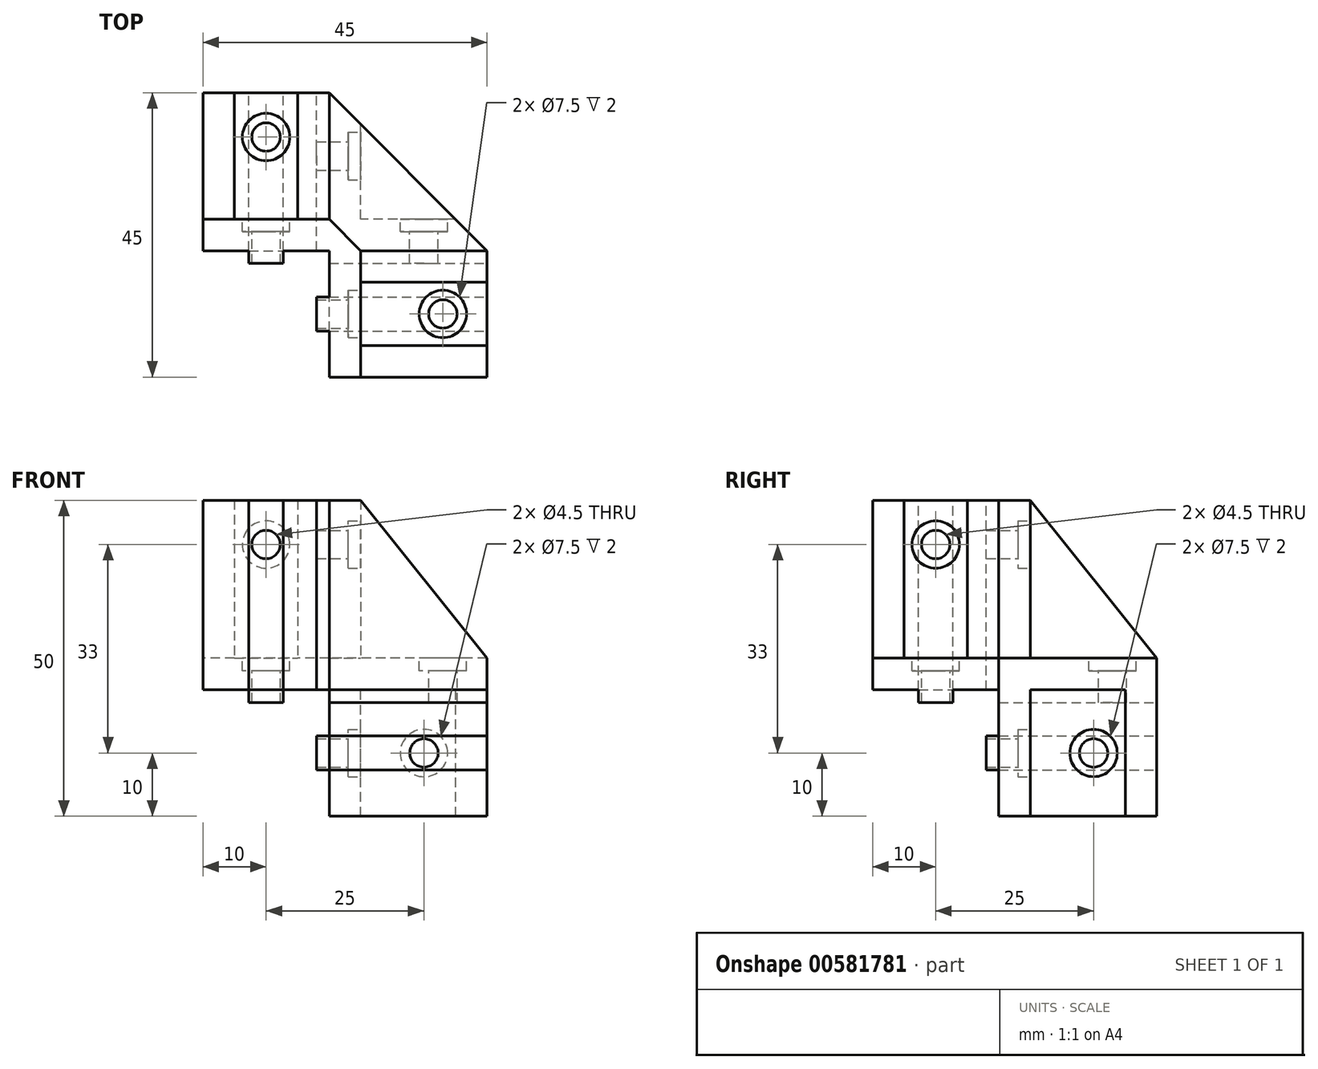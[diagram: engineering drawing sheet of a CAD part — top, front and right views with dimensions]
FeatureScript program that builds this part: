
annotation { "Feature Type Name" : "Feature", "Feature Type Description" : "" }
export const myFeature = defineFeature(function(context is Context, id is Id, definition is map)
    precondition{}
    {
        {
            var Q0;
            Q0=qCreatedBy(makeId("Top.planeOp"),FACE);
            var sketch = newSketch(context, id + "F0", { "sketchPlane" : qUnion([Q0])});
            skLineSegment(sketch, "E0", {"start": v(0, 0) * mm, "end": v(0, 60) * mm, "construction": true});
            skLineSegment(sketch, "E1", {"start": v(0, 60) * mm, "end": v(20, 60) * mm, "construction": true});
            skLineSegment(sketch, "E2", {"start": v(20, 60) * mm, "end": v(20, 20) * mm, "construction": true});
            skLineSegment(sketch, "E3", {"start": v(20, 20) * mm, "end": v(60, 20) * mm, "construction": true});
            skLineSegment(sketch, "E4", {"start": v(60, 20) * mm, "end": v(60, 0) * mm, "construction": true});
            skLineSegment(sketch, "E5", {"start": v(60, 0) * mm, "end": v(0, 0) * mm, "construction": true});
            skLineSegment(sketch, "E6", {"start": v(20, 20) * mm, "end": v(0, 20) * mm});
            skLineSegment(sketch, "E7", {"start": v(0, 20) * mm, "end": v(0, 45) * mm});
            skLineSegment(sketch, "E8", {"start": v(0, 45) * mm, "end": v(20, 45) * mm});
            skLineSegment(sketch, "E9", {"start": v(20, 20) * mm, "end": v(20, 0) * mm});
            skLineSegment(sketch, "E10", {"start": v(20, 0) * mm, "end": v(45, 0) * mm});
            skLineSegment(sketch, "E11", {"start": v(45, 0) * mm, "end": v(45, 20) * mm});
            skPoint(sketch, "E11.endSnap0", {"position": v(40, 20) * mm});
            skLineSegment(sketch, "E12", {"start": v(45, 20) * mm, "end": v(20, 45) * mm});
            skSolve(sketch);
        }
        {
            var Q0;
            Q0=makeQuery(id+"F0.imprint","IMPRINT",FACE,{"disambiguationData":[TD([[makeQuery(id+"F0.imprint","IMPRINT",EDGE,{"derivedFrom":sQuery(id+"F0.wireOp",EDGE,"E6")}),-1.0]])]});
            extrude(context, id + "F1", {"entities" : qUnion([Q0]), "depth" : 5 * mm});
        }
        {
            var Q0;
            Q0=makeQuery(id+"F1.opExtrude","CAP_FACE",FACE,{"disambiguationData":[OSD([sQuery(id+"F0.wireOp",EDGE,"E6"),sQuery(id+"F0.wireOp",EDGE,"E7"),sQuery(id+"F0.wireOp",EDGE,"E8"),sQuery(id+"F0.wireOp",EDGE,"E9"),sQuery(id+"F0.wireOp",EDGE,"E10"),sQuery(id+"F0.wireOp",EDGE,"E11"),sQuery(id+"F0.wireOp",EDGE,"E12")])],"isStart":false});
            var sketch = newSketch(context, id + "F2", { "sketchPlane" : qUnion([Q0])});
            skLineSegment(sketch, "E13", {"start": v(0, 20) * mm, "end": v(0, 25) * mm});
            skLineSegment(sketch, "E14", {"start": v(5, 25) * mm, "end": v(15, 25) * mm});
            skLineSegment(sketch, "E15", {"start": v(25, 15) * mm, "end": v(25, 5) * mm});
            skLineSegment(sketch, "E16", {"start": v(25, 0) * mm, "end": v(20, 0) * mm});
            skLineSegment(sketch, "E17", {"start": v(20, 0) * mm, "end": v(20, 20) * mm});
            skLineSegment(sketch, "E18", {"start": v(20, 20) * mm, "end": v(0, 20) * mm});
            skLineSegment(sketch, "E19", {"start": v(20, 45) * mm, "end": v(20, 25) * mm});
            skLineSegment(sketch, "E20", {"start": v(20, 45) * mm, "end": v(15, 45) * mm});
            skLineSegment(sketch, "E21", {"start": v(15, 45) * mm, "end": v(15, 25) * mm});
            skLineSegment(sketch, "E22", {"start": v(0, 25) * mm, "end": v(0, 45) * mm});
            skLineSegment(sketch, "E23", {"start": v(0, 45) * mm, "end": v(5, 45) * mm});
            skLineSegment(sketch, "E24", {"start": v(5, 45) * mm, "end": v(5, 25) * mm});
            skLineSegment(sketch, "E25", {"start": v(45, 20) * mm, "end": v(25, 20) * mm});
            skLineSegment(sketch, "E26", {"start": v(45, 20) * mm, "end": v(45, 15) * mm});
            skLineSegment(sketch, "E27", {"start": v(45, 15) * mm, "end": v(25, 15) * mm});
            skLineSegment(sketch, "E28", {"start": v(45, 0) * mm, "end": v(45, 5) * mm});
            skLineSegment(sketch, "E29", {"start": v(45, 5) * mm, "end": v(25, 5) * mm});
            skLineSegment(sketch, "E30", {"start": v(45, 0) * mm, "end": v(25, 0) * mm});
            skLineSegment(sketch, "E31", {"start": v(20, 25) * mm, "end": v(25, 20) * mm});
            skSolve(sketch);
        }
        {
            var Q0;
            Q0=qSketchRegion(id+"F2",true);
            extrude(context, id + "F3", {"entities" : qUnion([Q0]), "operationType" : NewBodyOperationType.ADD, "depth" : 25 * mm});
        }
        {
            var Q0;
            Q0=qSketchRegion(id+"F2",true);
            extrude(context, id + "F4", {"entities" : qUnion([Q0]), "operationType" : NewBodyOperationType.ADD, "depth" : 25 * mm});
        }
        {
            var Q0;
            Q0=makeQuery(id+"F3.boolean.opBoolean","MERGE",FACE,{"derivedFrom":[makeQuery(id+"F1.opExtrude","SWEPT_FACE",FACE,{"disambiguationData":[OSD([sQuery(id+"F0.wireOp",EDGE,"E7")])]}),makeQuery(id+"F3.opExtrude","SWEPT_FACE",FACE,{"disambiguationData":[OSD([sQuery(id+"F2.wireOp",EDGE,"E13"),sQuery(id+"F2.wireOp",EDGE,"E22")])]})]});
            var sketch = newSketch(context, id + "F5", { "sketchPlane" : qUnion([Q0])});
            skLineSegment(sketch, "E32", {"start": v(-20, 30) * mm, "end": v(-25, 30) * mm, "construction": true});
            skLineSegment(sketch, "E33", {"start": v(-45, 0) * mm, "end": v(-45, 5) * mm, "construction": true});
            skLineSegment(sketch, "E34", {"start": v(-45, 5) * mm, "end": v(-25, 30) * mm});
            skLineSegment(sketch, "E35", {"start": v(-25, 30) * mm, "end": v(-45, 30) * mm});
            skLineSegment(sketch, "E36", {"start": v(-45, 30) * mm, "end": v(-45, 5) * mm});
            skSolve(sketch);
        }
        {
            var Q0;
            Q0=qSketchRegion(id+"F5",true);
            extrude(context, id + "F6", {"entities" : qUnion([Q0]), "operationType" : NewBodyOperationType.REMOVE, "endBound" : BoundingType.THROUGH_ALL, "oppositeDirection" : true, "depth" : 25 * mm});
        }
        {
            var Q0;
            {var subQ0=sQuery(id+"F0.wireOp",EDGE,"E6");var subQ1=sQuery(id+"F11.wireOp",EDGE,"E47");var subQ2=sQuery(id+"F11.wireOp",EDGE,"E46");var subQ3=sQuery(id+"F11.wireOp",EDGE,"E45");var subQ4=makeQuery(id+"F12.opExtrude","CAP_FACE",FACE,{"disambiguationData":[OSD([sQuery(id+"F11.wireOp",EDGE,"E44"),subQ3,subQ2,subQ1,sQuery(id+"F11.wireOp",EDGE,"E48")])],"isStart":false});var subQ5=sQuery(id+"F0.wireOp",EDGE,"E9");var subQ6=sQuery(id+"F0.wireOp",EDGE,"E12");var subQ7=sQuery(id+"F0.wireOp",EDGE,"E8");var subQ8=sQuery(id+"F0.wireOp",EDGE,"E7");var subQ9=makeQuery(id+"F1.opExtrude","CAP_FACE",FACE,{"disambiguationData":[OSD([subQ0,subQ8,subQ7,subQ5,sQuery(id+"F0.wireOp",EDGE,"E10"),sQuery(id+"F0.wireOp",EDGE,"E11"),subQ6])],"isStart":true});var subQ10=makeQuery(id+"F12.opExtrude","CAP_FACE",FACE,{"disambiguationData":[OSD([sQuery(id+"F11.wireOp",EDGE,"E49"),sQuery(id+"F11.wireOp",EDGE,"E50"),sQuery(id+"F11.wireOp",EDGE,"E51"),sQuery(id+"F11.wireOp",EDGE,"E52"),sQuery(id+"F11.wireOp",EDGE,"E53")])],"isStart":false});Q0=makeQuery(id+"F20.boolean.opBoolean","SPLIT",FACE,{"disambiguationData":[TD([makeQuery(id+"F1.opExtrude","SWEPT_FACE",FACE,{"disambiguationData":[OSD([subQ8])]})])],"derivedFrom":makeQuery(id+"F12.boolean.opBoolean","MERGE",FACE,{"derivedFrom":[subQ9,subQ4,subQ10]})});}
            var sketch = newSketch(context, id + "F7", { "sketchPlane" : qUnion([Q0])});
            skLineSegment(sketch, "E37.bottom", {"start": v(18, -7.29) * mm, "end": v(45, -7.29) * mm});
            skLineSegment(sketch, "E37.top", {"start": v(18, -12.7) * mm, "end": v(45, -12.7) * mm});
            skLineSegment(sketch, "E37.left", {"start": v(18, -7.29) * mm, "end": v(18, -12.7) * mm});
            skLineSegment(sketch, "E37.right", {"start": v(45, -7.29) * mm, "end": v(45, -12.7) * mm});
            skPoint(sketch, "E38.oppositeSnap0", {"position": v(12.71, -19) * mm});
            skLineSegment(sketch, "E38.bottom", {"start": v(7.3, -18) * mm, "end": v(12.71, -18) * mm});
            skLineSegment(sketch, "E38.top", {"start": v(7.3, -45) * mm, "end": v(12.71, -45) * mm});
            skLineSegment(sketch, "E38.left", {"start": v(7.3, -18) * mm, "end": v(7.3, -45) * mm});
            skLineSegment(sketch, "E38.right", {"start": v(12.71, -18) * mm, "end": v(12.71, -45) * mm});
            skSolve(sketch);
        }
        {
            var Q0;
            Q0=qSketchRegion(id+"F7",true);
            extrude(context, id + "F8", {"entities" : qUnion([Q0]), "operationType" : NewBodyOperationType.ADD, "depth" : 2 * mm});
        }
        {
            var Q0;
            Q0=makeQuery(id+"F3.boolean.opBoolean","MERGE",FACE,{"derivedFrom":[makeQuery(id+"F1.opExtrude","SWEPT_FACE",FACE,{"disambiguationData":[OSD([sQuery(id+"F0.wireOp",EDGE,"E10")])]}),makeQuery(id+"F3.opExtrude","SWEPT_FACE",FACE,{"disambiguationData":[OSD([sQuery(id+"F2.wireOp",EDGE,"E16"),sQuery(id+"F2.wireOp",EDGE,"E30")])]})]});
            var sketch = newSketch(context, id + "F9", { "sketchPlane" : qUnion([Q0])});
            skLineSegment(sketch, "E39", {"start": v(20, 30) * mm, "end": v(25, 30) * mm, "construction": true});
            skLineSegment(sketch, "E40", {"start": v(25, 30) * mm, "end": v(45, 5) * mm});
            skLineSegment(sketch, "E41", {"start": v(45, 5) * mm, "end": v(45, 0) * mm, "construction": true});
            skLineSegment(sketch, "E42", {"start": v(25, 30) * mm, "end": v(45, 30) * mm});
            skLineSegment(sketch, "E43", {"start": v(45, 30) * mm, "end": v(45, 5) * mm});
            skSolve(sketch);
        }
        {
            var Q0;
            Q0=qSketchRegion(id+"F9",true);
            extrude(context, id + "F10", {"entities" : qUnion([Q0]), "operationType" : NewBodyOperationType.REMOVE, "endBound" : BoundingType.THROUGH_ALL, "oppositeDirection" : true, "depth" : 25 * mm});
        }
        {
            var Q0;
            Q0=makeQuery(id+"F3.opExtrude","CAP_FACE",FACE,{"disambiguationData":[OSD([sQuery(id+"F2.wireOp",EDGE,"E13"),sQuery(id+"F2.wireOp",EDGE,"E14"),sQuery(id+"F2.wireOp",EDGE,"E15"),sQuery(id+"F2.wireOp",EDGE,"E16"),sQuery(id+"F2.wireOp",EDGE,"E17"),sQuery(id+"F2.wireOp",EDGE,"E18"),sQuery(id+"F2.wireOp",EDGE,"E19"),sQuery(id+"F2.wireOp",EDGE,"E20"),sQuery(id+"F2.wireOp",EDGE,"E21"),sQuery(id+"F2.wireOp",EDGE,"E22"),sQuery(id+"F2.wireOp",EDGE,"E23"),sQuery(id+"F2.wireOp",EDGE,"E24"),sQuery(id+"F2.wireOp",EDGE,"E25"),sQuery(id+"F2.wireOp",EDGE,"E26"),sQuery(id+"F2.wireOp",EDGE,"E27"),sQuery(id+"F2.wireOp",EDGE,"E28"),sQuery(id+"F2.wireOp",EDGE,"E29"),sQuery(id+"F2.wireOp",EDGE,"E30"),sQuery(id+"F2.wireOp",EDGE,"E31")])],"isStart":false});
            var sketch = newSketch(context, id + "F11", { "sketchPlane" : qUnion([Q0])});
            skLineSegment(sketch, "E44", {"start": v(10, 20) * mm, "end": v(12.71, 20) * mm});
            skLineSegment(sketch, "E45", {"start": v(12.71, 20) * mm, "end": v(12.71, 18) * mm});
            skLineSegment(sketch, "E46", {"start": v(12.71, 18) * mm, "end": v(7.3, 18) * mm});
            skLineSegment(sketch, "E47", {"start": v(7.3, 18) * mm, "end": v(7.3, 20) * mm});
            skLineSegment(sketch, "E48", {"start": v(7.3, 20) * mm, "end": v(10, 20) * mm});
            skLineSegment(sketch, "E49", {"start": v(20, 10) * mm, "end": v(20, 12.7) * mm});
            skLineSegment(sketch, "E50", {"start": v(20, 12.7) * mm, "end": v(18, 12.7) * mm});
            skLineSegment(sketch, "E51", {"start": v(18, 12.7) * mm, "end": v(18, 7.29) * mm});
            skLineSegment(sketch, "E52", {"start": v(18, 7.29) * mm, "end": v(20, 7.29) * mm});
            skLineSegment(sketch, "E53", {"start": v(20, 7.29) * mm, "end": v(20, 10) * mm});
            skSolve(sketch);
        }
        {
            var Q0;
            Q0=qSketchRegion(id+"F11",true);
            extrude(context, id + "F12", {"entities" : qUnion([Q0]), "operationType" : NewBodyOperationType.ADD, "oppositeDirection" : true, "depth" : 30 * mm});
        }
        {
            var Q0;
            {var subQ0=sQuery(id+"F0.wireOp",EDGE,"E8");Q0=makeQuery(id+"F3.boolean.opBoolean","SPLIT",FACE,{"disambiguationData":[TD([makeQuery(id+"F3.opExtrude","SWEPT_FACE",FACE,{"disambiguationData":[OSD([sQuery(id+"F2.wireOp",EDGE,"E14")])]})])],"derivedFrom":makeQuery(id+"F1.opExtrude","CAP_FACE",FACE,{"disambiguationData":[OSD([sQuery(id+"F0.wireOp",EDGE,"E6"),sQuery(id+"F0.wireOp",EDGE,"E7"),subQ0,sQuery(id+"F0.wireOp",EDGE,"E9"),sQuery(id+"F0.wireOp",EDGE,"E10"),sQuery(id+"F0.wireOp",EDGE,"E11"),sQuery(id+"F0.wireOp",EDGE,"E12")])],"isStart":false})});}
            var sketch = newSketch(context, id + "F13", { "sketchPlane" : qUnion([Q0])});
            skCircle(sketch, "E54", {"center": v(10, 38) * mm, "radius": 2.25 * mm});
            skCircle(sketch, "E55", {"center": v(38, 10) * mm, "radius": 2.25 * mm});
            skSolve(sketch);
        }
        {
            var Q0;
            Q0=makeQuery(id+"F13.imprint","IMPRINT",FACE,{"disambiguationData":[TD([[makeQuery(id+"F13.imprint","IMPRINT",EDGE,{"derivedFrom":sQuery(id+"F13.wireOp",EDGE,"E54")}),1.0]])]});
            var Q1;
            Q1=makeQuery(id+"F13.imprint","IMPRINT",FACE,{"disambiguationData":[TD([[makeQuery(id+"F13.imprint","IMPRINT",EDGE,{"derivedFrom":sQuery(id+"F13.wireOp",EDGE,"E55")}),1.0]])]});
            extrude(context, id + "F14", {"entities" : qUnion([Q0, Q1]), "operationType" : NewBodyOperationType.REMOVE, "endBound" : BoundingType.THROUGH_ALL, "oppositeDirection" : true, "depth" : 25 * mm});
        }
        {
            var Q0;
            Q0=makeQuery(id+"F3.opExtrude","SWEPT_FACE",FACE,{"disambiguationData":[OSD([sQuery(id+"F2.wireOp",EDGE,"E14")])]});
            var sketch = newSketch(context, id + "F15", { "sketchPlane" : qUnion([Q0])});
            skCircle(sketch, "E56", {"center": v(-10, 23) * mm, "radius": 2.25 * mm});
            skSolve(sketch);
        }
        {
            var Q0;
            Q0=qSketchRegion(id+"F15",true);
            extrude(context, id + "F16", {"entities" : qUnion([Q0]), "operationType" : NewBodyOperationType.REMOVE, "endBound" : BoundingType.THROUGH_ALL, "oppositeDirection" : true, "depth" : 25 * mm});
        }
        {
            var Q0;
            Q0=makeQuery(id+"F3.opExtrude","SWEPT_FACE",FACE,{"disambiguationData":[OSD([sQuery(id+"F2.wireOp",EDGE,"E15")])]});
            var sketch = newSketch(context, id + "F17", { "sketchPlane" : qUnion([Q0])});
            skCircle(sketch, "E57", {"center": v(10, 23) * mm, "radius": 2.25 * mm});
            skSolve(sketch);
        }
        {
            var Q0;
            Q0=qSketchRegion(id+"F17",true);
            extrude(context, id + "F18", {"entities" : qUnion([Q0]), "operationType" : NewBodyOperationType.REMOVE, "endBound" : BoundingType.THROUGH_ALL, "oppositeDirection" : true, "depth" : 25 * mm});
        }
        {
            var Q0;
            Q0=makeQuery(id+"F1.opExtrude","CAP_FACE",FACE,{"disambiguationData":[OSD([sQuery(id+"F0.wireOp",EDGE,"E6"),sQuery(id+"F0.wireOp",EDGE,"E7"),sQuery(id+"F0.wireOp",EDGE,"E8"),sQuery(id+"F0.wireOp",EDGE,"E9"),sQuery(id+"F0.wireOp",EDGE,"E10"),sQuery(id+"F0.wireOp",EDGE,"E11"),sQuery(id+"F0.wireOp",EDGE,"E12")])],"isStart":true});
            var sketch = newSketch(context, id + "F19", { "sketchPlane" : qUnion([Q0])});
            skLineSegment(sketch, "E58", {"start": v(45, -20) * mm, "end": v(20, -20) * mm});
            skLineSegment(sketch, "E59", {"start": v(20, -20) * mm, "end": v(20, -45) * mm});
            skLineSegment(sketch, "E60", {"start": v(45, -20) * mm, "end": v(40, -25) * mm});
            skLineSegment(sketch, "E61", {"start": v(40, -25) * mm, "end": v(25, -25) * mm});
            skLineSegment(sketch, "E62", {"start": v(25, -25) * mm, "end": v(25, -40) * mm});
            skLineSegment(sketch, "E63", {"start": v(25, -40) * mm, "end": v(20, -45) * mm});
            skSolve(sketch);
        }
        {
            var Q0;
            Q0=qSketchRegion(id+"F19",true);
            extrude(context, id + "F20", {"entities" : qUnion([Q0]), "operationType" : NewBodyOperationType.ADD, "depth" : 20 * mm});
        }
        {
            var Q0;
            Q0=makeQuery(id+"F20.opExtrude","SWEPT_FACE",FACE,{"disambiguationData":[OSD([sQuery(id+"F19.wireOp",EDGE,"E58")])]});
            var sketch = newSketch(context, id + "F21", { "sketchPlane" : qUnion([Q0])});
            skLineSegment(sketch, "E64", {"start": v(45, -10) * mm, "end": v(45, -12.71) * mm});
            skLineSegment(sketch, "E65", {"start": v(45, -12.71) * mm, "end": v(20, -12.71) * mm});
            skLineSegment(sketch, "E66", {"start": v(20, -12.71) * mm, "end": v(20, -7.3) * mm});
            skLineSegment(sketch, "E67", {"start": v(20, -7.3) * mm, "end": v(45, -7.3) * mm});
            skLineSegment(sketch, "E68", {"start": v(45, -7.3) * mm, "end": v(45, -10) * mm});
            skSolve(sketch);
        }
        {
            var Q0;
            Q0=qSketchRegion(id+"F21",true);
            extrude(context, id + "F22", {"entities" : qUnion([Q0]), "operationType" : NewBodyOperationType.ADD, "depth" : 2 * mm});
        }
        {
            var Q0;
            Q0=makeQuery(id+"F22.boolean.opBoolean","MERGE",FACE,{"derivedFrom":[makeQuery(id+"F20.opExtrude","SWEPT_FACE",FACE,{"disambiguationData":[OSD([sQuery(id+"F19.wireOp",EDGE,"E59")])]}),makeQuery(id+"F22.opExtrude","SWEPT_FACE",FACE,{"disambiguationData":[OSD([sQuery(id+"F21.wireOp",EDGE,"E66")])]})]});
            var sketch = newSketch(context, id + "F23", { "sketchPlane" : qUnion([Q0])});
            skLineSegment(sketch, "E69.bottom", {"start": v(-18, -12.71) * mm, "end": v(-45, -12.71) * mm});
            skLineSegment(sketch, "E69.top", {"start": v(-18, -7.3) * mm, "end": v(-45, -7.3) * mm});
            skLineSegment(sketch, "E69.left", {"start": v(-18, -12.71) * mm, "end": v(-18, -7.3) * mm});
            skLineSegment(sketch, "E69.right", {"start": v(-45, -12.71) * mm, "end": v(-45, -7.3) * mm});
            skSolve(sketch);
        }
        {
            var Q0;
            Q0=qSketchRegion(id+"F23",true);
            extrude(context, id + "F24", {"entities" : qUnion([Q0]), "operationType" : NewBodyOperationType.ADD, "depth" : 2 * mm});
        }
        {
            var Q0;
            Q0=makeQuery(id+"F20.opExtrude","SWEPT_FACE",FACE,{"disambiguationData":[OSD([sQuery(id+"F19.wireOp",EDGE,"E62")])]});
            var sketch = newSketch(context, id + "F25", { "sketchPlane" : qUnion([Q0])});
            skCircle(sketch, "E70", {"center": v(35, -10) * mm, "radius": 2.25 * mm});
            skPoint(sketch, "E70.centerSnap0", {"position": v(40, -10) * mm});
            skSolve(sketch);
        }
        {
            var Q0;
            Q0=qSketchRegion(id+"F25",true);
            extrude(context, id + "F26", {"entities" : qUnion([Q0]), "operationType" : NewBodyOperationType.REMOVE, "endBound" : BoundingType.THROUGH_ALL, "oppositeDirection" : true, "depth" : 25 * mm});
        }
        {
            var Q0;
            Q0=makeQuery(id+"F20.opExtrude","SWEPT_FACE",FACE,{"disambiguationData":[OSD([sQuery(id+"F19.wireOp",EDGE,"E61")])]});
            var sketch = newSketch(context, id + "F27", { "sketchPlane" : qUnion([Q0])});
            skCircle(sketch, "E71", {"center": v(-35, -10) * mm, "radius": 2.25 * mm});
            skPoint(sketch, "E71.centerSnap0", {"position": v(-40, -10) * mm});
            skSolve(sketch);
        }
        {
            var Q0;
            Q0=makeQuery(id+"F27.imprint","IMPRINT",FACE,{"disambiguationData":[TD([[makeQuery(id+"F27.imprint","IMPRINT",EDGE,{"derivedFrom":sQuery(id+"F27.wireOp",EDGE,"E71")}),1.0]])]});
            extrude(context, id + "F28", {"entities" : qUnion([Q0]), "operationType" : NewBodyOperationType.REMOVE, "endBound" : BoundingType.THROUGH_ALL, "oppositeDirection" : true, "depth" : 25 * mm});
        }
        {
            var Q0;
            Q0=makeQuery(id+"F20.opExtrude","SWEPT_FACE",FACE,{"disambiguationData":[OSD([sQuery(id+"F19.wireOp",EDGE,"E61")])]});
            var sketch = newSketch(context, id + "F29", { "sketchPlane" : qUnion([Q0])});
            skCircle(sketch, "E72", {"center": v(-35, -10) * mm, "radius": 3.75 * mm});
            skSolve(sketch);
        }
        {
            var Q0;
            Q0=qSketchRegion(id+"F29",true);
            extrude(context, id + "F30", {"entities" : qUnion([Q0]), "operationType" : NewBodyOperationType.REMOVE, "oppositeDirection" : true, "depth" : 2 * mm});
        }
        {
            var Q0;
            Q0=makeQuery(id+"F20.opExtrude","SWEPT_FACE",FACE,{"disambiguationData":[OSD([sQuery(id+"F19.wireOp",EDGE,"E62")])]});
            var sketch = newSketch(context, id + "F31", { "sketchPlane" : qUnion([Q0])});
            skCircle(sketch, "E73", {"center": v(35, -10) * mm, "radius": 3.75 * mm});
            skSolve(sketch);
        }
        {
            var Q0;
            Q0=qSketchRegion(id+"F31",true);
            extrude(context, id + "F32", {"entities" : qUnion([Q0]), "operationType" : NewBodyOperationType.REMOVE, "oppositeDirection" : true, "depth" : 2 * mm});
        }
        {
            var Q0;
            Q0=makeQuery(id+"F3.opExtrude","SWEPT_FACE",FACE,{"disambiguationData":[OSD([sQuery(id+"F2.wireOp",EDGE,"E14")])]});
            var sketch = newSketch(context, id + "F33", { "sketchPlane" : qUnion([Q0])});
            skCircle(sketch, "E74", {"center": v(-10, 23) * mm, "radius": 3.75 * mm});
            skSolve(sketch);
        }
        {
            var Q0;
            Q0=qSketchRegion(id+"F33",true);
            extrude(context, id + "F34", {"entities" : qUnion([Q0]), "operationType" : NewBodyOperationType.REMOVE, "oppositeDirection" : true, "depth" : 2 * mm});
        }
        {
            var Q0;
            Q0=makeQuery(id+"F3.opExtrude","SWEPT_FACE",FACE,{"disambiguationData":[OSD([sQuery(id+"F2.wireOp",EDGE,"E15")])]});
            var sketch = newSketch(context, id + "F35", { "sketchPlane" : qUnion([Q0])});
            skCircle(sketch, "E75", {"center": v(10, 23) * mm, "radius": 3.75 * mm});
            skSolve(sketch);
        }
        {
            var Q0;
            Q0=qSketchRegion(id+"F35",true);
            extrude(context, id + "F36", {"entities" : qUnion([Q0]), "operationType" : NewBodyOperationType.REMOVE, "oppositeDirection" : true, "depth" : 2 * mm});
        }
        {
            var Q0;
            {var subQ0=sQuery(id+"F0.wireOp",EDGE,"E11");Q0=makeQuery(id+"F3.boolean.opBoolean","SPLIT",FACE,{"disambiguationData":[TD([makeQuery(id+"F3.opExtrude","SWEPT_FACE",FACE,{"disambiguationData":[OSD([sQuery(id+"F2.wireOp",EDGE,"E15")])]})])],"derivedFrom":makeQuery(id+"F1.opExtrude","CAP_FACE",FACE,{"disambiguationData":[OSD([sQuery(id+"F0.wireOp",EDGE,"E6"),sQuery(id+"F0.wireOp",EDGE,"E7"),sQuery(id+"F0.wireOp",EDGE,"E8"),sQuery(id+"F0.wireOp",EDGE,"E9"),sQuery(id+"F0.wireOp",EDGE,"E10"),subQ0,sQuery(id+"F0.wireOp",EDGE,"E12")])],"isStart":false})});}
            var sketch = newSketch(context, id + "F37", { "sketchPlane" : qUnion([Q0])});
            skCircle(sketch, "E76", {"center": v(38, 10) * mm, "radius": 3.75 * mm});
            skSolve(sketch);
        }
        {
            var Q0;
            Q0=qSketchRegion(id+"F37",true);
            extrude(context, id + "F38", {"entities" : qUnion([Q0]), "operationType" : NewBodyOperationType.REMOVE, "oppositeDirection" : true, "depth" : 2 * mm});
        }
        {
            var Q0;
            {var subQ0=sQuery(id+"F0.wireOp",EDGE,"E8");Q0=makeQuery(id+"F3.boolean.opBoolean","SPLIT",FACE,{"disambiguationData":[TD([makeQuery(id+"F3.opExtrude","SWEPT_FACE",FACE,{"disambiguationData":[OSD([sQuery(id+"F2.wireOp",EDGE,"E14")])]})])],"derivedFrom":makeQuery(id+"F1.opExtrude","CAP_FACE",FACE,{"disambiguationData":[OSD([sQuery(id+"F0.wireOp",EDGE,"E6"),sQuery(id+"F0.wireOp",EDGE,"E7"),subQ0,sQuery(id+"F0.wireOp",EDGE,"E9"),sQuery(id+"F0.wireOp",EDGE,"E10"),sQuery(id+"F0.wireOp",EDGE,"E11"),sQuery(id+"F0.wireOp",EDGE,"E12")])],"isStart":false})});}
            var sketch = newSketch(context, id + "F39", { "sketchPlane" : qUnion([Q0])});
            skCircle(sketch, "E77", {"center": v(10, 38) * mm, "radius": 3.75 * mm});
            skSolve(sketch);
        }
        {
            var Q0;
            Q0=qSketchRegion(id+"F39",true);
            extrude(context, id + "F40", {"entities" : qUnion([Q0]), "operationType" : NewBodyOperationType.REMOVE, "oppositeDirection" : true, "depth" : 2 * mm});
        }
        {
            var Q0;
            Q0=makeQuery(id+"F24.boolean.opBoolean","MERGE",FACE,{"derivedFrom":[makeQuery(id+"F22.opExtrude","SWEPT_FACE",FACE,{"disambiguationData":[OSD([sQuery(id+"F21.wireOp",EDGE,"E67")])]}),makeQuery(id+"F24.opExtrude","SWEPT_FACE",FACE,{"disambiguationData":[OSD([sQuery(id+"F23.wireOp",EDGE,"E69.top")])]})]});
            var sketch = newSketch(context, id + "F41", { "sketchPlane" : qUnion([Q0])});
            skLineSegment(sketch, "E78.bottom", {"start": v(20, 20) * mm, "end": v(18, 20) * mm});
            skLineSegment(sketch, "E78.top", {"start": v(20, 18) * mm, "end": v(18, 18) * mm});
            skLineSegment(sketch, "E78.left", {"start": v(20, 20) * mm, "end": v(20, 18) * mm});
            skLineSegment(sketch, "E78.right", {"start": v(18, 20) * mm, "end": v(18, 18) * mm});
            skSolve(sketch);
        }
        {
            var Q0;
            Q0=qSketchRegion(id+"F41",true);
            extrude(context, id + "F42", {"entities" : qUnion([Q0]), "operationType" : NewBodyOperationType.REMOVE, "endBound" : BoundingType.THROUGH_ALL, "oppositeDirection" : true, "depth" : 25 * mm});
        }
        {
            var Q0;
            Q0=makeQuery(id+"F12.boolean.opBoolean","MERGE",FACE,{"derivedFrom":[makeQuery(id+"F8.opExtrude","SWEPT_FACE",FACE,{"disambiguationData":[OSD([sQuery(id+"F7.wireOp",EDGE,"E38.right")])]}),makeQuery(id+"F12.opExtrude","SWEPT_FACE",FACE,{"disambiguationData":[OSD([sQuery(id+"F11.wireOp",EDGE,"E45")])]})]});
            var sketch = newSketch(context, id + "F43", { "sketchPlane" : qUnion([Q0])});
            skLineSegment(sketch, "E79.bottom", {"start": v(20, 0) * mm, "end": v(18, 0) * mm});
            skLineSegment(sketch, "E79.top", {"start": v(20, -2) * mm, "end": v(18, -2) * mm});
            skLineSegment(sketch, "E79.left", {"start": v(20, 0) * mm, "end": v(20, -2) * mm});
            skLineSegment(sketch, "E79.right", {"start": v(18, 0) * mm, "end": v(18, -2) * mm});
            skSolve(sketch);
        }
        {
            var Q0;
            Q0=qSketchRegion(id+"F43",true);
            extrude(context, id + "F44", {"entities" : qUnion([Q0]), "operationType" : NewBodyOperationType.REMOVE, "endBound" : BoundingType.THROUGH_ALL, "oppositeDirection" : true, "depth" : 25 * mm});
        }
        {
            var Q0;
            Q0=makeQuery(id+"F12.boolean.opBoolean","MERGE",FACE,{"derivedFrom":[makeQuery(id+"F8.opExtrude","SWEPT_FACE",FACE,{"disambiguationData":[OSD([sQuery(id+"F7.wireOp",EDGE,"E37.top")])]}),makeQuery(id+"F12.opExtrude","SWEPT_FACE",FACE,{"disambiguationData":[OSD([sQuery(id+"F11.wireOp",EDGE,"E50")])]})]});
            var sketch = newSketch(context, id + "F45", { "sketchPlane" : qUnion([Q0])});
            skLineSegment(sketch, "E80.bottom", {"start": v(-20, 0) * mm, "end": v(-18, 0) * mm});
            skLineSegment(sketch, "E80.top", {"start": v(-20, -2) * mm, "end": v(-18, -2) * mm});
            skLineSegment(sketch, "E80.left", {"start": v(-20, 0) * mm, "end": v(-20, -2) * mm});
            skLineSegment(sketch, "E80.right", {"start": v(-18, 0) * mm, "end": v(-18, -2) * mm});
            skSolve(sketch);
        }
        {
            var Q0;
            Q0=qSketchRegion(id+"F45",true);
            extrude(context, id + "F46", {"entities" : qUnion([Q0]), "operationType" : NewBodyOperationType.REMOVE, "endBound" : BoundingType.THROUGH_ALL, "oppositeDirection" : true, "depth" : 25 * mm});
        }
    });
